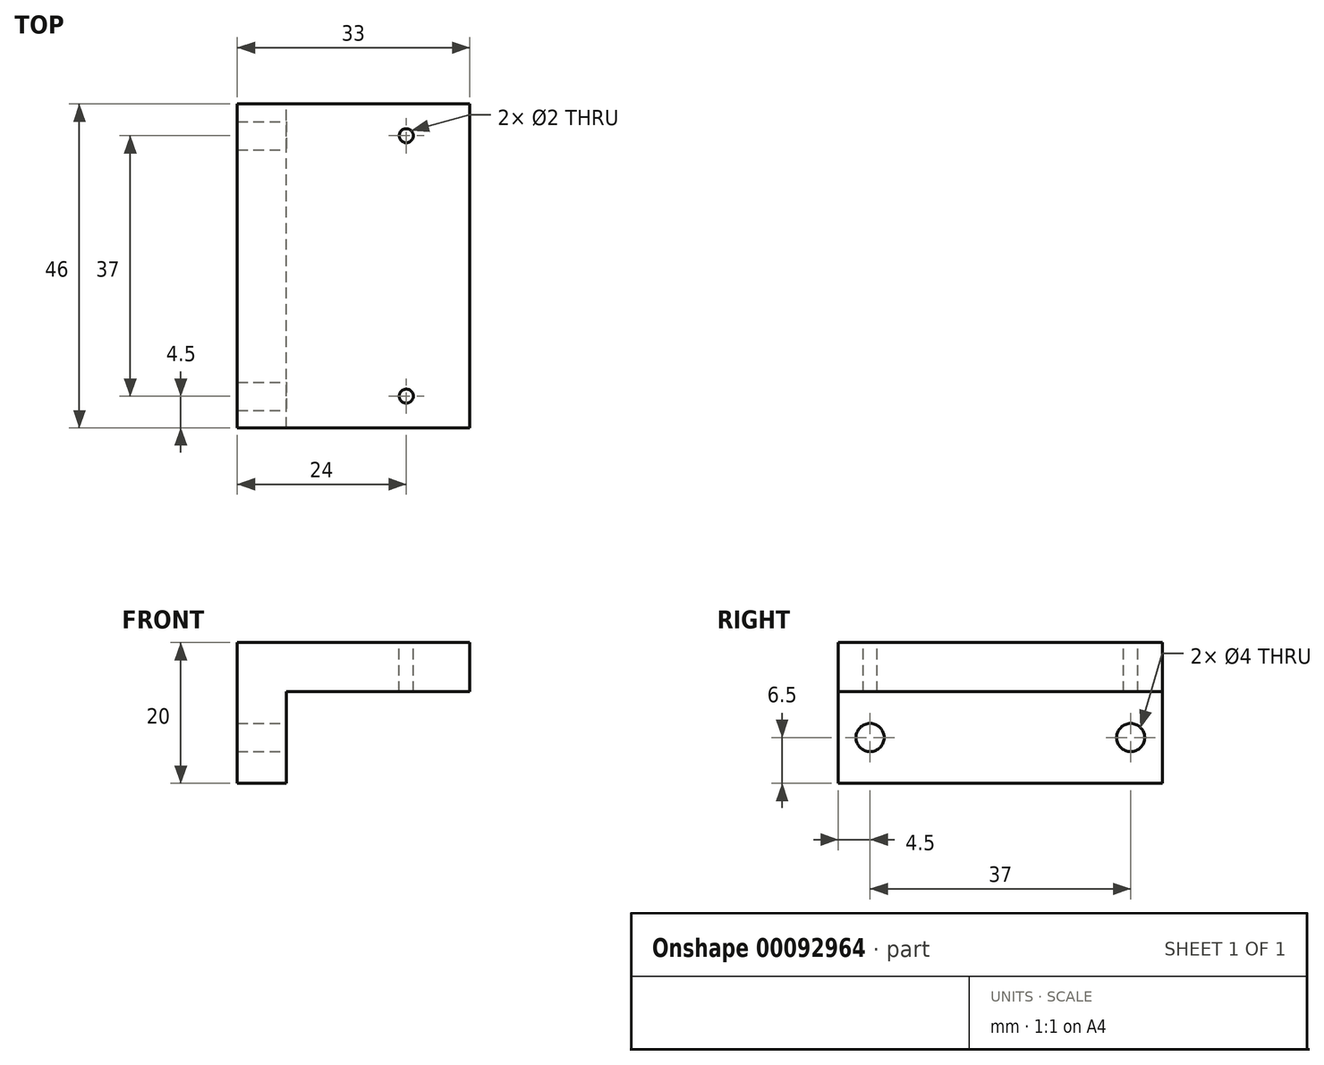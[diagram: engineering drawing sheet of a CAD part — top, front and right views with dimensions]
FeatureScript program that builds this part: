
annotation { "Feature Type Name" : "Feature", "Feature Type Description" : "" }
export const myFeature = defineFeature(function(context is Context, id is Id, definition is map)
    precondition{}
    {
        {
            var Q0;
            Q0=qCreatedBy(makeId("Front.planeOp"),FACE);
            var sketch = newSketch(context, id + "F0", { "sketchPlane" : qUnion([Q0])});
            skLineSegment(sketch, "E0", {"start": v(0, 0) * mm, "end": v(0, -20) * mm});
            skLineSegment(sketch, "E1", {"start": v(0, -20) * mm, "end": v(7, -20) * mm});
            skLineSegment(sketch, "E2", {"start": v(7, -20) * mm, "end": v(7, -7) * mm});
            skLineSegment(sketch, "E3", {"start": v(7, -7) * mm, "end": v(33, -7) * mm});
            skLineSegment(sketch, "E4", {"start": v(33, -7) * mm, "end": v(33, 0) * mm});
            skLineSegment(sketch, "E5", {"start": v(33, 0) * mm, "end": v(0, 0) * mm});
            skSolve(sketch);
        }
        {
            var Q0;
            Q0=makeQuery(id+"F0.imprint","IMPRINT",FACE,{"disambiguationData":[TD([[makeQuery(id+"F0.imprint","IMPRINT",EDGE,{"derivedFrom":sQuery(id+"F0.wireOp",EDGE,"E0")}),1.0]])]});
            extrude(context, id + "F1", {"entities" : qUnion([Q0]), "depth" : 46 * mm});
        }
        {
            var Q0;
            Q0=makeQuery(id+"F1.opExtrude","SWEPT_FACE",FACE,{"disambiguationData":[OSD([sQuery(id+"F0.wireOp",EDGE,"E5")])]});
            var sketch = newSketch(context, id + "F2", { "sketchPlane" : qUnion([Q0])});
            skLineSegment(sketch, "E6", {"start": v(24, 0) * mm, "end": v(24, -46) * mm, "construction": true});
            skCircle(sketch, "E7", {"center": v(24, -4.5) * mm, "radius": 1 * mm});
            skCircle(sketch, "E8", {"center": v(24, -41.5) * mm, "radius": 1 * mm});
            skSolve(sketch);
        }
        {
            var Q0;
            Q0=makeQuery(id+"F2.imprint","IMPRINT",FACE,{"disambiguationData":[TD([[makeQuery(id+"F2.imprint","IMPRINT",EDGE,{"derivedFrom":sQuery(id+"F2.wireOp",EDGE,"E7")}),1.0]])]});
            var Q1;
            Q1=makeQuery(id+"F2.imprint","IMPRINT",FACE,{"disambiguationData":[TD([[makeQuery(id+"F2.imprint","IMPRINT",EDGE,{"derivedFrom":sQuery(id+"F2.wireOp",EDGE,"E8")}),1.0]])]});
            extrude(context, id + "F3", {"entities" : qUnion([Q0, Q1]), "operationType" : NewBodyOperationType.REMOVE, "endBound" : BoundingType.THROUGH_ALL, "oppositeDirection" : true, "depth" : 25 * mm});
        }
        {
            var Q0;
            Q0=makeQuery(id+"F1.opExtrude","SWEPT_FACE",FACE,{"disambiguationData":[OSD([sQuery(id+"F0.wireOp",EDGE,"E2")])]});
            var sketch = newSketch(context, id + "F4", { "sketchPlane" : qUnion([Q0])});
            skLineSegment(sketch, "E9", {"start": v(-46, -13.5) * mm, "end": v(0, -13.5) * mm, "construction": true});
            skPoint(sketch, "E10", {"position": v(-41.5, -13.5) * mm});
            skPoint(sketch, "E11", {"position": v(-4.5, -13.5) * mm});
            skSolve(sketch);
        }
        {
            var Q0;
            Q0=sQuery(id+"F4.wireOp",VERTEX,"E10");
            var Q1;
            Q1=sQuery(id+"F4.wireOp",VERTEX,"E11");
            var Q2;
            Q2=makeQuery(id+"F1.opExtrude","SWEPT_BODY",BODY,{"disambiguationData":[OSD([sQuery(id+"F0.wireOp",EDGE,"E0"),sQuery(id+"F0.wireOp",EDGE,"E1"),sQuery(id+"F0.wireOp",EDGE,"E2"),sQuery(id+"F0.wireOp",EDGE,"E3"),sQuery(id+"F0.wireOp",EDGE,"E4"),sQuery(id+"F0.wireOp",EDGE,"E5")])]});
            hole(context, id + "F5", {"style" : HoleStyle.SIMPLE, "endStyle" : HoleEndStyle.THROUGH, "holeDiameter" : 4 * mm, "locations" : qUnion([Q0, Q1]), "scope" : qUnion([Q2]), "isTappedThrough" : true});
        }
    });
